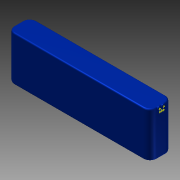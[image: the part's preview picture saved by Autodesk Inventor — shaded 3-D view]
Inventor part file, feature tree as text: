
AUTODESK INVENTOR PART (.ipt)
format: ipt  version: 2011 SP1 (Build 150282100, 282)  size: 157,184 bytes
history: native  units: in
note: dims shown in document units (in); Inventor stores cm internally (conversion verified against a paired STEP export)
features: sketch x7, extrude x2, fillet x2, other x2
ambient origin geometry x8: Origin, YZ Plane, XZ Plane, XY Plane, X Axis, Y Axis, Z Axis, Center Point
bodies: Solid1 (feature_tree)
feature tree (13):
  extrude  "Extrusion1"  Depth=5.3in
  extrude  "Extrusion2"  Depth=0.153in
  fillet  "Fillet1"  Radius=0.061in
  fillet  "Fillet2"  Radius=0.01in
  sketch  "Sketch3"  dims[d8=0.25in]
  sketch  "Sketch4"  dims[d9=0.05in]
  sketch  "Sketch5"
  sketch  "Sketch6"
  other  "s1-"
  sketch  "Sketch7"
  other  "s2-"
  sketch  "Sketch1"  dims[d0=1.67in d1=5.3in]
  sketch  "Sketch2"  dims[d2=0.823in d3=0.0in d4=0.153in d5=0.061in d6=0.01in d7=0.0in]
